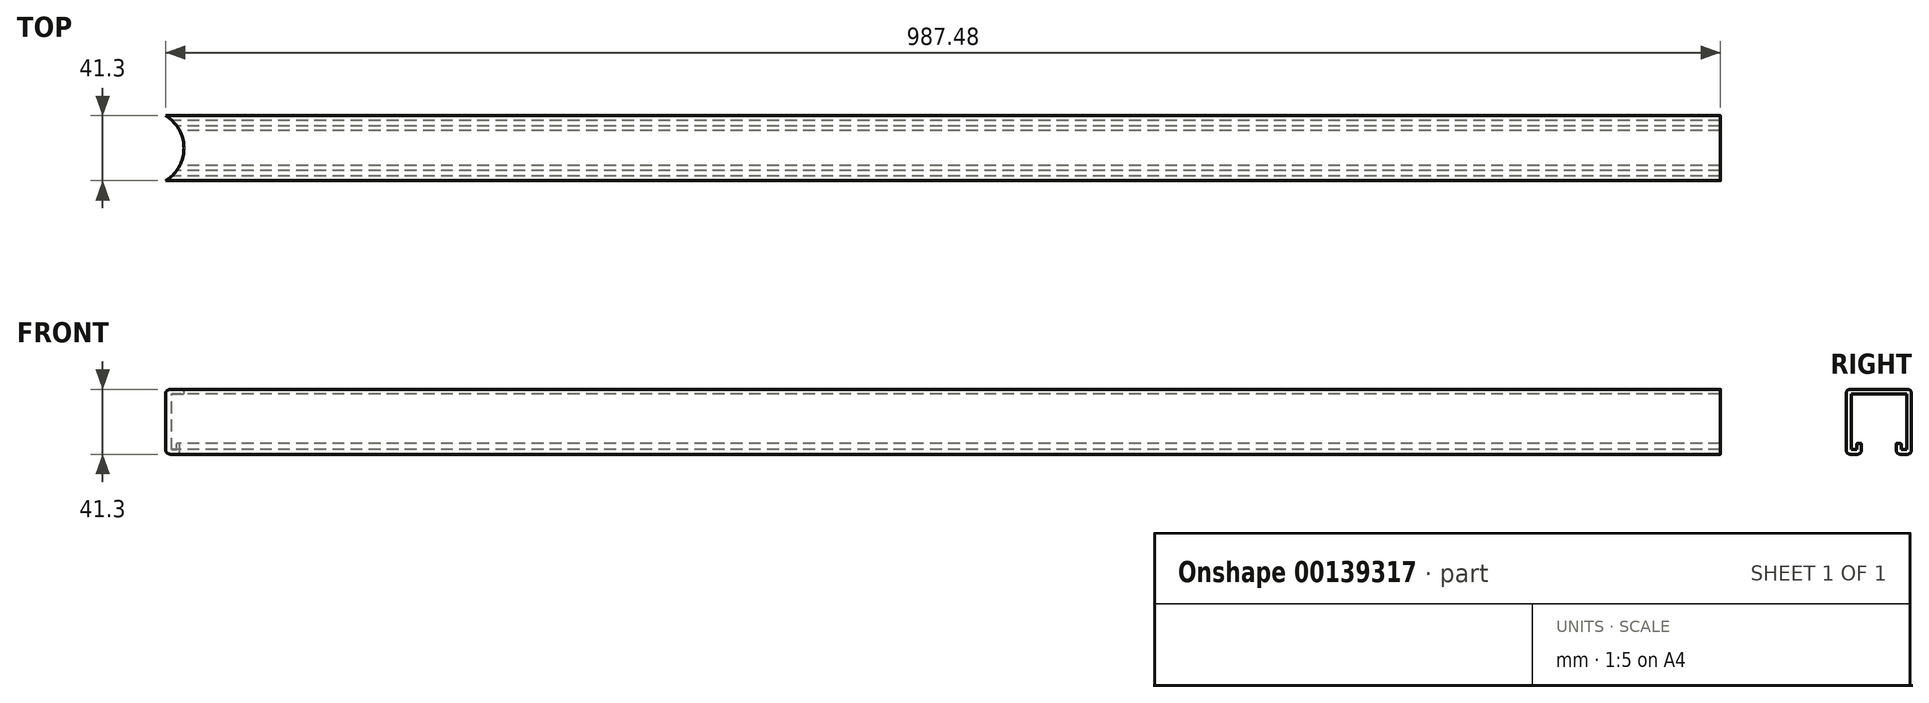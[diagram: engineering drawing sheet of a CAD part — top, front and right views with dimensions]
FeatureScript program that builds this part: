
annotation { "Feature Type Name" : "Feature", "Feature Type Description" : "" }
export const myFeature = defineFeature(function(context is Context, id is Id, definition is map)
    precondition{}
    {
        {
            var Q0;
            Q0=qCreatedBy(makeId("Right.planeOp"),FACE);
            var sketch = newSketch(context, id + "F0", { "sketchPlane" : qUnion([Q0])});
            skLineSegment(sketch, "E0", {"start": v(0, 2.5) * mm, "end": v(0, 38.8) * mm});
            skLineSegment(sketch, "E1", {"start": v(2.5, 41.3) * mm, "end": v(38.8, 41.3) * mm});
            skLineSegment(sketch, "E2", {"start": v(41.3, 38.8) * mm, "end": v(41.3, 2.5) * mm});
            skLineSegment(sketch, "E3", {"start": v(38.8, 0) * mm, "end": v(34.25, 0) * mm});
            skLineSegment(sketch, "E4", {"start": v(2.5, 0) * mm, "end": v(7.05, 0) * mm});
            skLineSegment(sketch, "E5.0", {"start": v(38.3, 3) * mm, "end": v(34.75, 3) * mm});
            skLineSegment(sketch, "E5.1", {"start": v(3, 3) * mm, "end": v(6.55, 3) * mm});
            skLineSegment(sketch, "E5.2", {"start": v(3, 3) * mm, "end": v(3, 38.3) * mm});
            skLineSegment(sketch, "E5.3", {"start": v(3, 38.3) * mm, "end": v(38.3, 38.3) * mm});
            skLineSegment(sketch, "E5.4", {"start": v(38.3, 38.3) * mm, "end": v(38.3, 3) * mm});
            skLineSegment(sketch, "E6", {"start": v(9.55, 2.5) * mm, "end": v(9.55, 3) * mm});
            skLineSegment(sketch, "E7", {"start": v(31.75, 2.5) * mm, "end": v(31.75, 3) * mm});
            skPoint(sketch, "E8.visualSharp", {"position": v(0, 41.3) * mm});
            skArc(sketch, "E8.filletArc", {"start": v(2.5, 41.3) * mm, "mid": v(0.73, 40.57) * mm, "end": v(0, 38.8) * mm});
            skPoint(sketch, "E9.visualSharp", {"position": v(0, 0) * mm});
            skArc(sketch, "E9.filletArc", {"start": v(0, 2.5) * mm, "mid": v(0.73, 0.73) * mm, "end": v(2.5, 0) * mm});
            skPoint(sketch, "E10.visualSharp", {"position": v(41.3, 0) * mm});
            skArc(sketch, "E10.filletArc", {"start": v(38.8, 0) * mm, "mid": v(40.57, 0.73) * mm, "end": v(41.3, 2.5) * mm});
            skPoint(sketch, "E11.visualSharp", {"position": v(41.3, 41.3) * mm});
            skArc(sketch, "E11.filletArc", {"start": v(41.3, 38.8) * mm, "mid": v(40.57, 40.57) * mm, "end": v(38.8, 41.3) * mm});
            skLineSegment(sketch, "E12", {"start": v(9.55, 3) * mm, "end": v(9.55, 6.5) * mm});
            skLineSegment(sketch, "E13", {"start": v(31.75, 3) * mm, "end": v(31.75, 6.5) * mm});
            skLineSegment(sketch, "E14", {"start": v(32.25, 7) * mm, "end": v(34.25, 7) * mm});
            skLineSegment(sketch, "E15", {"start": v(34.75, 6.5) * mm, "end": v(34.75, 3) * mm});
            skLineSegment(sketch, "E16", {"start": v(9.05, 7) * mm, "end": v(7.05, 7) * mm});
            skLineSegment(sketch, "E17", {"start": v(6.55, 6.5) * mm, "end": v(6.55, 3) * mm});
            skPoint(sketch, "E18.visualSharp", {"position": v(9.55, 0) * mm});
            skArc(sketch, "E18.filletArc", {"start": v(7.05, 0) * mm, "mid": v(8.82, 0.73) * mm, "end": v(9.55, 2.5) * mm});
            skPoint(sketch, "E19.visualSharp", {"position": v(31.75, 0) * mm});
            skArc(sketch, "E19.filletArc", {"start": v(31.75, 2.5) * mm, "mid": v(32.48, 0.73) * mm, "end": v(34.25, 0) * mm});
            skPoint(sketch, "E20.visualSharp", {"position": v(9.55, 7) * mm});
            skArc(sketch, "E20.filletArc", {"start": v(9.55, 6.5) * mm, "mid": v(9.4, 6.85) * mm, "end": v(9.05, 7) * mm});
            skPoint(sketch, "E21.visualSharp", {"position": v(6.55, 7) * mm});
            skArc(sketch, "E21.filletArc", {"start": v(7.05, 7) * mm, "mid": v(6.7, 6.85) * mm, "end": v(6.55, 6.5) * mm});
            skPoint(sketch, "E22.visualSharp", {"position": v(31.75, 7) * mm});
            skArc(sketch, "E22.filletArc", {"start": v(32.25, 7) * mm, "mid": v(31.9, 6.85) * mm, "end": v(31.75, 6.5) * mm});
            skPoint(sketch, "E23.visualSharp", {"position": v(34.75, 7) * mm});
            skArc(sketch, "E23.filletArc", {"start": v(34.75, 6.5) * mm, "mid": v(34.6, 6.85) * mm, "end": v(34.25, 7) * mm});
            skSolve(sketch);
        }
        {
            var Q0;
            Q0=makeQuery(id+"F0.imprint","IMPRINT",FACE,{"disambiguationData":[TD([[makeQuery(id+"F0.imprint","IMPRINT",EDGE,{"derivedFrom":sQuery(id+"F0.wireOp",EDGE,"E0")}),-1.0]])]});
            extrude(context, id + "F1", {"entities" : qUnion([Q0]), "depth" : 1000 * mm});
        }
        {
            var Q0;
            Q0=makeQuery(id+"F1.opExtrude","SWEPT_FACE",FACE,{"disambiguationData":[OSD([sQuery(id+"F0.wireOp",EDGE,"E1")])]});
            var sketch = newSketch(context, id + "F2", { "sketchPlane" : qUnion([Q0])});
            skCircle(sketch, "E24", {"center": v(0, 20.65) * mm, "radius": 24.15 * mm});
            skSolve(sketch);
        }
        {
            var Q0;
            Q0 = qSketchRegion(id + "F2", true);
            extrude(context, id + "F3", {"entities" : qUnion([Q0]), "operationType" : NewBodyOperationType.REMOVE, "endBound" : BoundingType.THROUGH_ALL, "oppositeDirection" : true, "depth" : 25 * mm});
        }
    });
